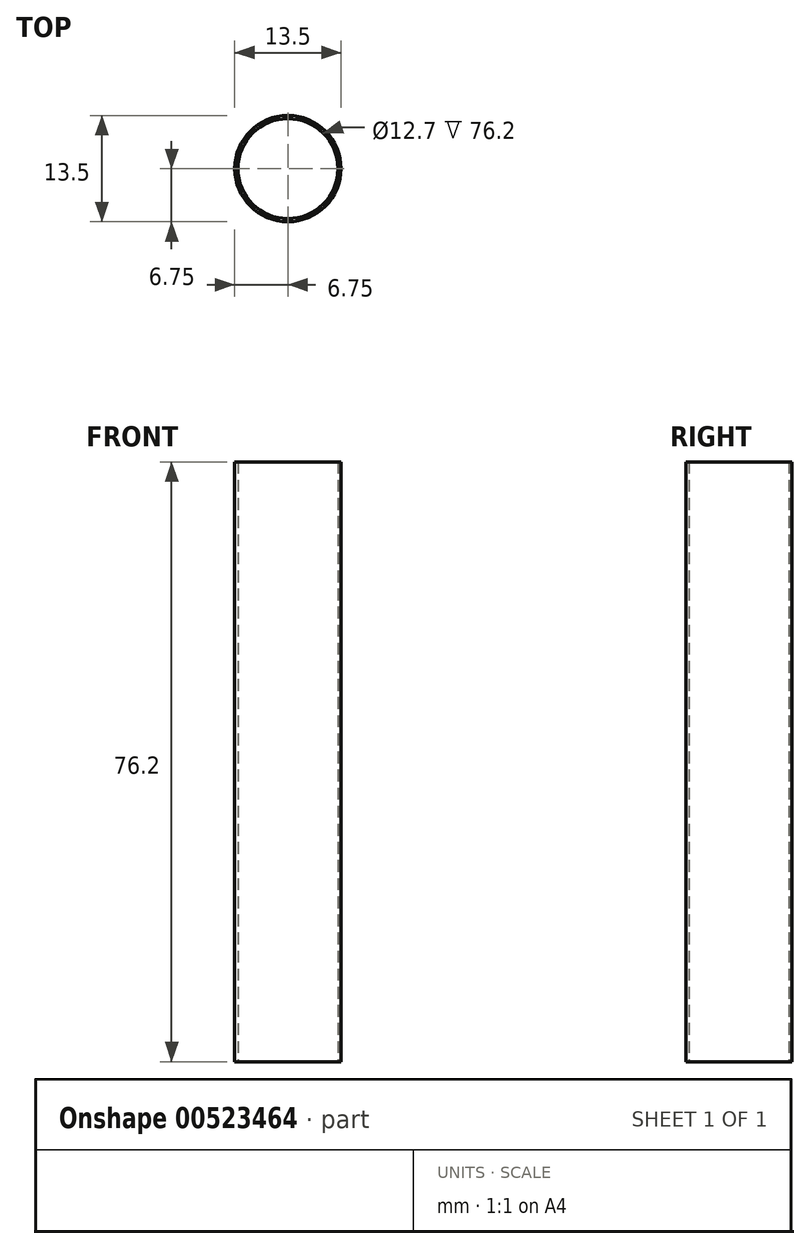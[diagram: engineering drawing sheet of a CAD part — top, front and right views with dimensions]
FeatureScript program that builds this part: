
annotation { "Feature Type Name" : "Feature", "Feature Type Description" : "" }
export const myFeature = defineFeature(function(context is Context, id is Id, definition is map)
    precondition{}
    {
        {
            var Q0;
            Q0=qCreatedBy(makeId("Top.planeOp"),FACE);
            var sketch = newSketch(context, id + "F0", { "sketchPlane" : qUnion([Q0])});
            skCircle(sketch, "E0", {"center": v(0, 0) * mm, "radius": 6.75 * mm});
            skSolve(sketch);
        }
        {
            var Q0;
            Q0=makeQuery(id+"F0.imprint","IMPRINT",FACE,{"disambiguationData":[TD([[makeQuery(id+"F0.imprint","IMPRINT",EDGE,{"derivedFrom":sQuery(id+"F0.wireOp",EDGE,"E0")}),1.0]])]});
            extrude(context, id + "F1", {"entities" : qUnion([Q0]), "depth" : 76.2 * mm, "offsetDistance" : 25.4 * mm});
        }
        {
            var Q0;
            Q0=makeQuery(id+"F1.opExtrude","CAP_FACE",FACE,{"disambiguationData":[OSD([sQuery(id+"F0.wireOp",EDGE,"E0")])],"isStart":true});
            var sketch = newSketch(context, id + "F2", { "sketchPlane" : qUnion([Q0])});
            skPoint(sketch, "E1.0", {"position": v(0, 0) * mm});
            skCircle(sketch, "E2", {"center": v(0, 0) * mm, "radius": 6.35 * mm});
            skSolve(sketch);
        }
        {
            var Q0;
            Q0 = qSketchRegion(id + "F2", true);
            extrude(context, id + "F3", {"entities" : qUnion([Q0]), "operationType" : NewBodyOperationType.REMOVE, "oppositeDirection" : true, "depth" : 76.2 * mm, "offsetDistance" : 25.4 * mm});
        }
    });
